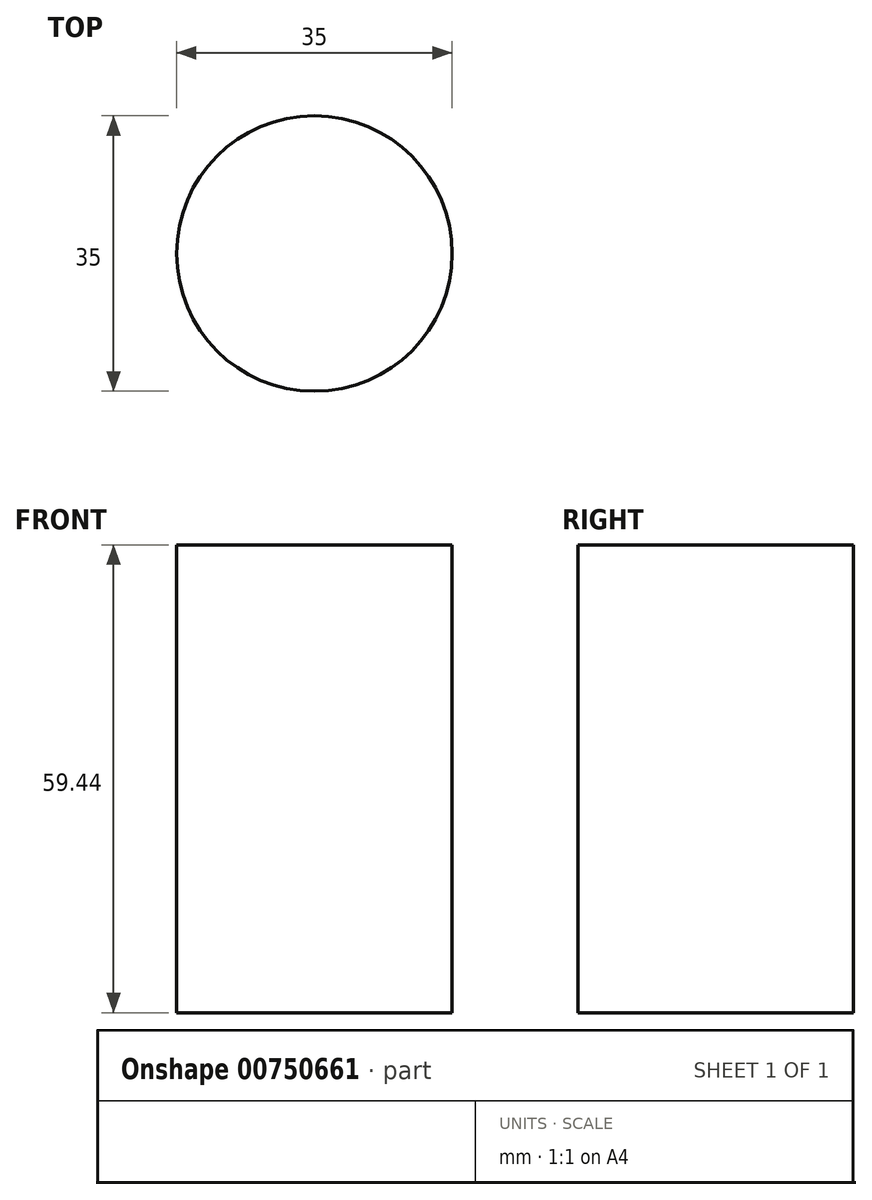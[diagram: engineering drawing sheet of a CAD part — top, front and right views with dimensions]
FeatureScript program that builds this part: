
annotation { "Feature Type Name" : "Feature", "Feature Type Description" : "" }
export const myFeature = defineFeature(function(context is Context, id is Id, definition is map)
    precondition{}
    {
        {
            var Q0;
            Q0=qCreatedBy(makeId("Top.planeOp"),FACE);
            var sketch = newSketch(context, id + "F0", { "sketchPlane" : qUnion([Q0])});
            skLineSegment(sketch, "E0.bottom", {"start": v(-51.48, 0) * mm, "end": v(0, 0) * mm});
            skLineSegment(sketch, "E0.top", {"start": v(-51.48, 325.06) * mm, "end": v(0, 325.06) * mm});
            skLineSegment(sketch, "E0.left", {"start": v(-51.48, 0) * mm, "end": v(-51.48, 325.06) * mm});
            skLineSegment(sketch, "E0.right", {"start": v(0, 0) * mm, "end": v(0, 325.06) * mm});
            skCircle(sketch, "E1", {"center": v(-29.07, 162.53) * mm, "radius": 17.5 * mm});
            skPoint(sketch, "E1.centerSnap0", {"position": v(-51.48, 162.53) * mm});
            skSolve(sketch);
        }
        {
            var Q0;
            Q0=makeQuery(id+"F0.imprint","IMPRINT",FACE,{"disambiguationData":[TD([[makeQuery(id+"F0.imprint","IMPRINT",EDGE,{"derivedFrom":sQuery(id+"F0.wireOp",EDGE,"E1")}),1.0]])]});
            extrude(context, id + "F1", {"entities" : qUnion([Q0]), "depth" : 59.44 * mm, "offsetDistance" : 25.4 * mm});
        }
    });
